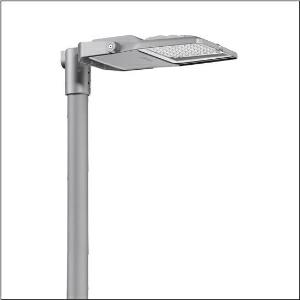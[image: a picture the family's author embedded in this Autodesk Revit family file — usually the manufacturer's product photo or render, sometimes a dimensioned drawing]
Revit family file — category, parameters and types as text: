
# Revit family: floodlight_fl_21_iq_mini___pl61_5xa7771d2c3a_41a8
name_source: partatom
category: Lighting Fixtures
units: mm (PartAtom-declared; Revit-internal decimal feet)

## family parameters
Cut with Voids When Loaded = No
Host = Face
Light Source = No
Part Type = Normal
Room Calculation Point = No
Round Connector Dimension = Use Diameter
Shared = No

## types (1)
- --- (1 x LED, 17500 lm, 143 W, 3000K)
    Apparent Load = 143 VA
    CIE Flux Codes = 33 65 98 100 100
    Color Rendering = 70
    Color Temperature = 3000K
    Default Elevation = 1800 mm
    Description = Floodlight FL 21 iQ mini, floodlight, primary light control with lens, of PMMA, primary optical cover: protective disc, of toughened safety glass, transparent, light distribution: PL61, light emission: direct distribution, installation type: surface-mounted, LED, High Power LED, rated luminous flux: 17.500lm, luminous efficacy: 122lm/W, light colour: 730, colour temperature: 3000K, control: Auto-Match, Temp-Guard, Lumen-Switch, Night-Set, Smart-Wire, Light-Fading, Desk-Remote (wireless, voltage-free reading and setting of iQ features in the workshop via application-optimized NFC function/RFID function), optimised constant luminous flux control (CLO 2.0), with terminal, 6-pole, mains connection: 220..240V, AC, 50/60Hz, start of lifetime: 143W, end of service life: 152W, reduction: 61W, luminaire housing, of diecast aluminium, powder-coated, Siteco® metallic grey (DB 702S), corrosivity category C5 mid according to DIN EN ISO 12944, sealing non-destructively replaceable, please order mast flange separately, mast bracket, of steel, galvanised, powder-coated, Siteco® metallic grey (DB 702S), protection rating (complete): IP66, insulation class (complete): insulation class II (safety insulation), certification: CE, ENEC, VDE, protection symbol: D, impact resistance: IK08, permissible operating ambient temperature: -40..+40°C, permissible operating ambient temperature for outdoor applications: -40..+50°C, standard: DIN EN 12944, LABS conformity tested according to VDMA 24364:2018-05, packaging unit: 1 piece

Light Distribution: PL61
    Height = 70 mm
    Lamp = 1 x LED
    Lamp Light Flux = 17500 lm
    Lamp Power = 143 W
    Lamp count = 1
    Length = 485 mm
    Luminous efficacy = 122 lm/W
    Manufacturer = Siteco
    ModVariant = No
    Model = 5XA7771D2C3A
    Number of Poles = 1
    OnlyDefault = Yes
    Power Factor = 1
    Product Name = Floodlight FL 21 iQ mini | PL61
    Product group = floodlight | pylon annexe
    ProductGroupID = 6200
    Protection Class = Protection class II
    Protection Degree = IP 66
    RLX_Detail_Level = 1
    RLX_Emergency_Light_Flux = 0 lm
    RLX_Emergency_Type = 0
    RLX_Emergency_Type_DB = No
    RlxData = <blob elided: 101621 chars, md5=414d1dba>
    Socket = socket
    Standby Power = 0 W
    System Light Flux = 17500 lm
    System Power = 143 W
    Type Comments = factory setting: luminous flux: 100 % | dim-lin: 254 | 730 mA
    Type Image = l_1007125.jpg
    URL = http://relux.com
    VarID = @adj_143827
    Voltage = 0 V
    Weight = 0.00 kg
    Width = 337 mm

## geometry (parser evidence)
native form markers: Blend x4, Sweep x11
no freeform markers — native parametric forms only
